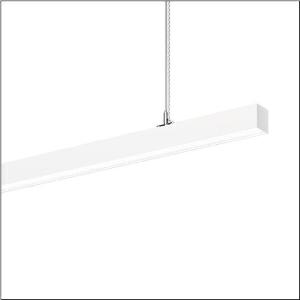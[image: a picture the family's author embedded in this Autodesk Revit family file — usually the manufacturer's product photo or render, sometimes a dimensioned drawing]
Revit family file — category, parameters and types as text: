
# Revit family: silica_r__21_51mx30db35wb_0444
name_source: partatom
category: Lighting Fixtures
units: mm (PartAtom-declared; Revit-internal decimal feet)

## family parameters
Cut with Voids When Loaded = No
Host = Face
Light Source = No
Part Type = Normal
Room Calculation Point = No
Round Connector Dimension = Use Diameter
Shared = No

## types (1)
- --- (1 x LED, 5260 lm, 34.1 W, 3000K)
    Apparent Load = 34 VA
    CIE Flux Codes = 47 79 96 57 100
    Color Rendering = 80
    Color Temperature = 3000K
    Default Elevation = 1800 mm
    Description = Silica® 21, office luminaire, primary optical cover: cover, of PMMA, opal, light emission: direct/indirect distribution, primary light characteristic: symmetric, installation type: suspended mounting, LED, rated luminous flux: 5.260lm, luminous efficacy: 154lm/W, light colour: 830, colour temperature: 3000K, with terminal, 3+2-pole, max. 2.5mm², mains connection: 220..240V, AC, 50/60Hz, rated input power: 34.1W, luminaire housing, of aluminium, traffic white (RAL 9016), length: 1.504mm, width: 53mm, height: 53mm, protection rating (complete): IP20, insulation class (complete): insulation class I (protective earthing), certification: CE, permissible operating ambient temperature: 0..+35°C, standard: EN 50419, packaging unit: 1 piece
    Height = 53 mm
    Lamp = 1 x LED
    Lamp Light Flux = 5260 lm
    Lamp Power = 34.1 W
    Lamp count = 1
    Length = 1504 mm
    Luminous efficacy = 154 lm/W
    Manufacturer = Siteco
    ModVariant = No
    Model = 51MX30DB35WB
    Mounting Place = Ceiling
    Mounting Type = Pendant
    Number of Poles = 1
    OnlyDefault = Yes
    Power Factor = 1
    Product Name = Silica® 21
    Product group = office luminaire | ceiling pendant
    ProductGroupID = 902
    Protection Class = Protection class I
    Protection Degree = IP 20
    RLX_Detail_Level = 1
    RLX_Emergency_Light_Flux = 0 lm
    RLX_Emergency_Type = 0
    RLX_Emergency_Type_DB = No
    RlxData = <blob elided: 21485 chars, md5=721e5f49>
    Socket = socket
    Standby Power = 0 W
    System Light Flux = 5260 lm
    System Power = 34 W
    Type Comments = factory setting: luminous flux: 100 % | dim-lin: 254 | 233 mA
    Type Image = l_1297784.jpg
    URL = http://relux.com
    VarID = @adj_046891
    Voltage = 0 V
    Weight = 0.00 kg
    Width = 53 mm

## geometry (parser evidence)
native form markers: Blend x4, Sweep x13
no freeform markers — native parametric forms only
